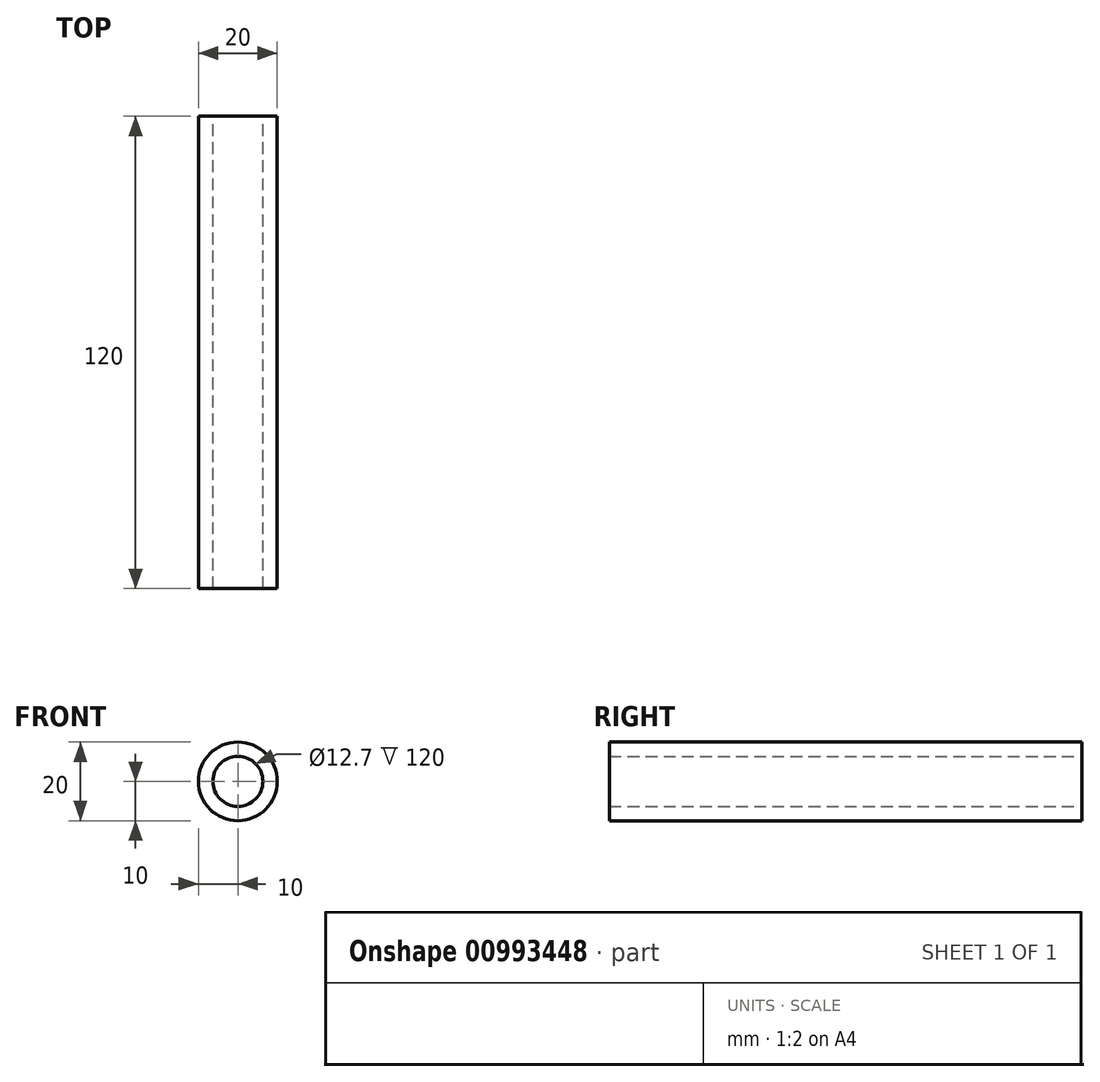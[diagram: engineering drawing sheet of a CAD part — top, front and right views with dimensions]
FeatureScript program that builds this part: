
annotation { "Feature Type Name" : "Feature", "Feature Type Description" : "" }
export const myFeature = defineFeature(function(context is Context, id is Id, definition is map)
    precondition{}
    {
        {
            var Q0;
            Q0=qCreatedBy(makeId("Front.planeOp"),FACE);
            var sketch = newSketch(context, id + "F0", { "sketchPlane" : qUnion([Q0])});
            skCircle(sketch, "E0", {"center": v(0, 0) * mm, "radius": 6.35 * mm});
            skCircle(sketch, "E1", {"center": v(0, 0) * mm, "radius": 10 * mm});
            skSolve(sketch);
        }
        {
            var Q0;
            Q0=makeQuery(id+"F0.imprint","IMPRINT",FACE,{"disambiguationData":[TD([[makeQuery(id+"F0.imprint","IMPRINT",EDGE,{"derivedFrom":sQuery(id+"F0.wireOp",EDGE,"E0")}),-1.0]])]});
            extrude(context, id + "F1", {"entities" : qUnion([Q0]), "depth" : 120 * mm, "offsetDistance" : 25 * mm});
        }
    });
